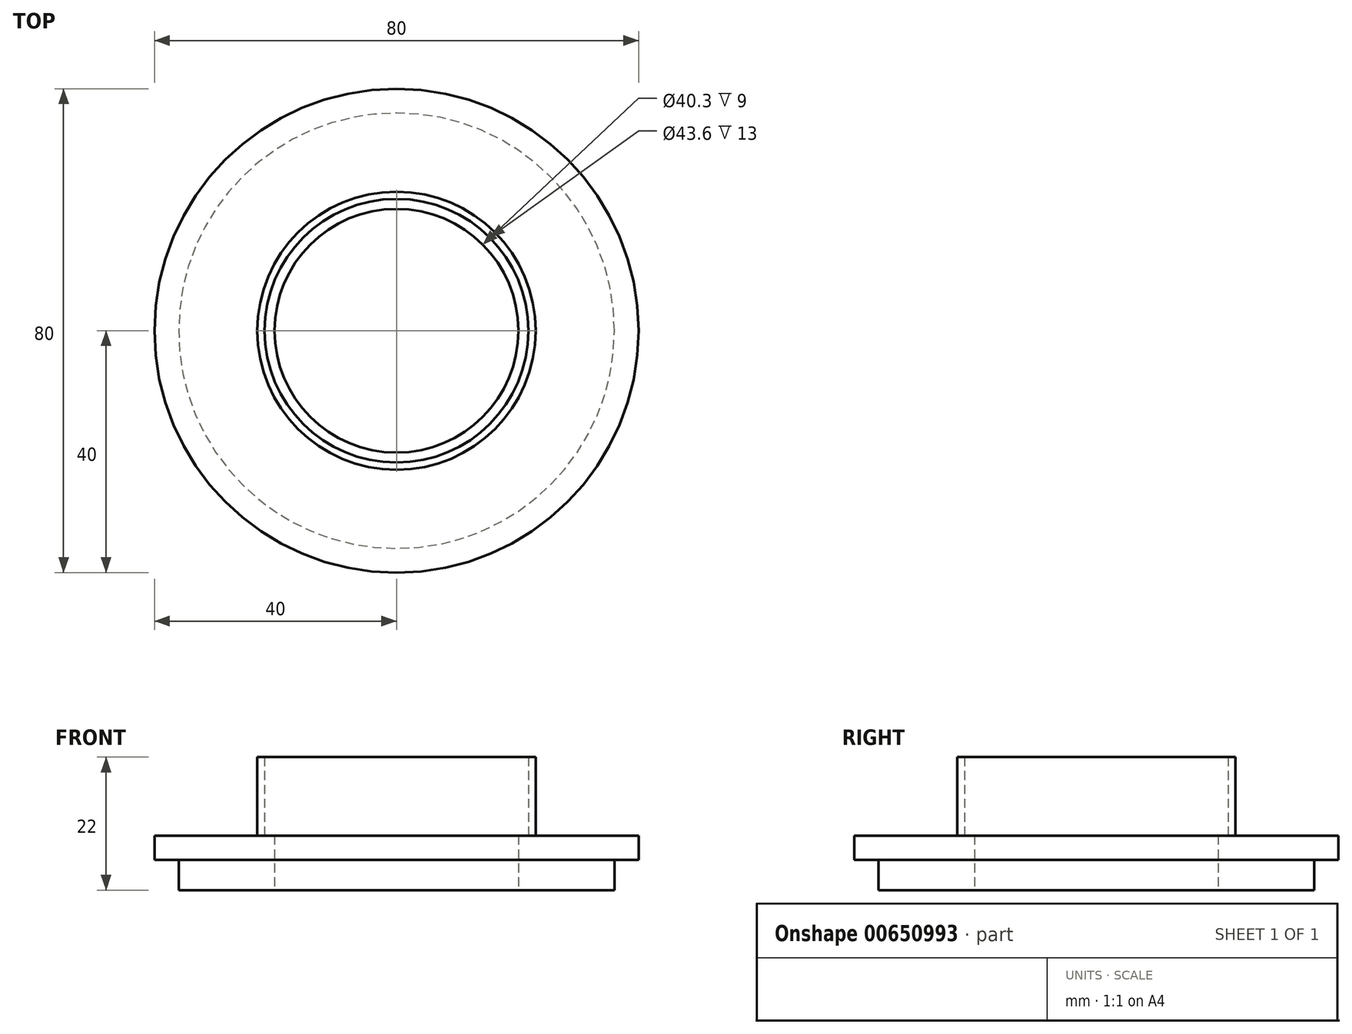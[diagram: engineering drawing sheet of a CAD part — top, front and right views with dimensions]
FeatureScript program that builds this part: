
annotation { "Feature Type Name" : "Feature", "Feature Type Description" : "" }
export const myFeature = defineFeature(function(context is Context, id is Id, definition is map)
    precondition{}
    {
        {
            var Q0;
            Q0=qCreatedBy(makeId("Front.planeOp"),FACE);
            var sketch = newSketch(context, id + "F0", { "sketchPlane" : qUnion([Q0])});
            skLineSegment(sketch, "E0.bottom", {"start": v(0, 0) * mm, "end": v(36, 0) * mm});
            skLineSegment(sketch, "E0.top", {"start": v(0, 5) * mm, "end": v(36, 5) * mm});
            skLineSegment(sketch, "E0.left", {"start": v(0, 0) * mm, "end": v(0, 5) * mm});
            skLineSegment(sketch, "E0.right", {"start": v(36, 0) * mm, "end": v(36, 5) * mm});
            skLineSegment(sketch, "E1.bottom", {"start": v(0, 5) * mm, "end": v(40, 5) * mm});
            skLineSegment(sketch, "E1.top", {"start": v(0, 9) * mm, "end": v(40, 9) * mm});
            skLineSegment(sketch, "E1.left", {"start": v(0, 5) * mm, "end": v(0, 9) * mm});
            skLineSegment(sketch, "E1.right", {"start": v(40, 5) * mm, "end": v(40, 9) * mm});
            skLineSegment(sketch, "E2.bottom", {"start": v(21.8, 9) * mm, "end": v(23, 9) * mm});
            skLineSegment(sketch, "E2.top", {"start": v(21.8, 22) * mm, "end": v(23, 22) * mm});
            skLineSegment(sketch, "E2.left", {"start": v(21.8, 9) * mm, "end": v(21.8, 22) * mm});
            skLineSegment(sketch, "E2.right", {"start": v(23, 9) * mm, "end": v(23, 22) * mm});
            skLineSegment(sketch, "E3", {"start": v(21.8, 9) * mm, "end": v(21.8, 0) * mm});
            skLineSegment(sketch, "E4.bottom", {"start": v(21.8, 0) * mm, "end": v(20.15, 0) * mm});
            skLineSegment(sketch, "E4.top", {"start": v(21.8, 22) * mm, "end": v(20.15, 22) * mm});
            skLineSegment(sketch, "E4.left", {"start": v(21.8, 0) * mm, "end": v(21.8, 22) * mm});
            skLineSegment(sketch, "E4.right", {"start": v(20.15, 0) * mm, "end": v(20.15, 22) * mm});
            skSolve(sketch);
        }
        {
            var Q0;
            {var subQ3=sQuery(id+"F0.wireOp",EDGE,"E0.right");Q0=makeQuery(id+"F0.imprint","IMPRINT",FACE,{"disambiguationData":[TD([[makeQuery(id+"F0.imprint","IMPRINT",EDGE,{"derivedFrom":subQ3}),1.0]])]});}
            var Q1;
            {var subQ5=sQuery(id+"F0.wireOp",EDGE,"E1.bottom");Q1=makeQuery(id+"F0.imprint","IMPRINT",FACE,{"disambiguationData":[TD([[makeQuery(id+"F0.imprint","IMPRINT",EDGE,{"derivedFrom":subQ5}),1.0]])]});}
            var Q2;
            {var subQ0=sQuery(id+"F0.wireOp",EDGE,"E3");var subQ1=sQuery(id+"F0.wireOp",EDGE,"E0.top");var subQ2=makeQuery(id+"F0.imprint","INTERSECT",VERTEX,{"derivedFrom":[subQ1,subQ0]});Q2=makeQuery(id+"F0.imprint","IMPRINT",FACE,{"disambiguationData":[TD([[makeQuery(id+"F0.imprint","IMPRINT",EDGE,{"disambiguationData":[TD([[subQ2,1.0]])],"derivedFrom":subQ1}),1.0]])]});}
            var Q3;
            {var subQ0=sQuery(id+"F0.wireOp",EDGE,"E3");var subQ1=sQuery(id+"F0.wireOp",EDGE,"E0.bottom");var subQ2=makeQuery(id+"F0.imprint","INTERSECT",VERTEX,{"derivedFrom":[subQ1,subQ0]});Q3=makeQuery(id+"F0.imprint","IMPRINT",FACE,{"disambiguationData":[TD([[makeQuery(id+"F0.imprint","IMPRINT",EDGE,{"disambiguationData":[TD([[subQ2,1.0]])],"derivedFrom":subQ1}),1.0]])]});}
            var Q4;
            Q4=makeQuery(id+"F0.imprint","IMPRINT",FACE,{"disambiguationData":[TD([[makeQuery(id+"F0.imprint","IMPRINT",EDGE,{"derivedFrom":sQuery(id+"F0.wireOp",EDGE,"E2.top")}),-1.0]])]});
            var Q5;
            Q5=sQuery(id+"F0.wireOp",EDGE,"E0.left");
            revolve(context, id + "F1", {"surfaceOperationType" : NewSurfaceOperationType.NEW, "entities" : qUnion([Q0, Q1, Q2, Q3, Q4]), "axis" : qUnion([Q5]), "revolveType" : RevolveType.FULL});
        }
    });
